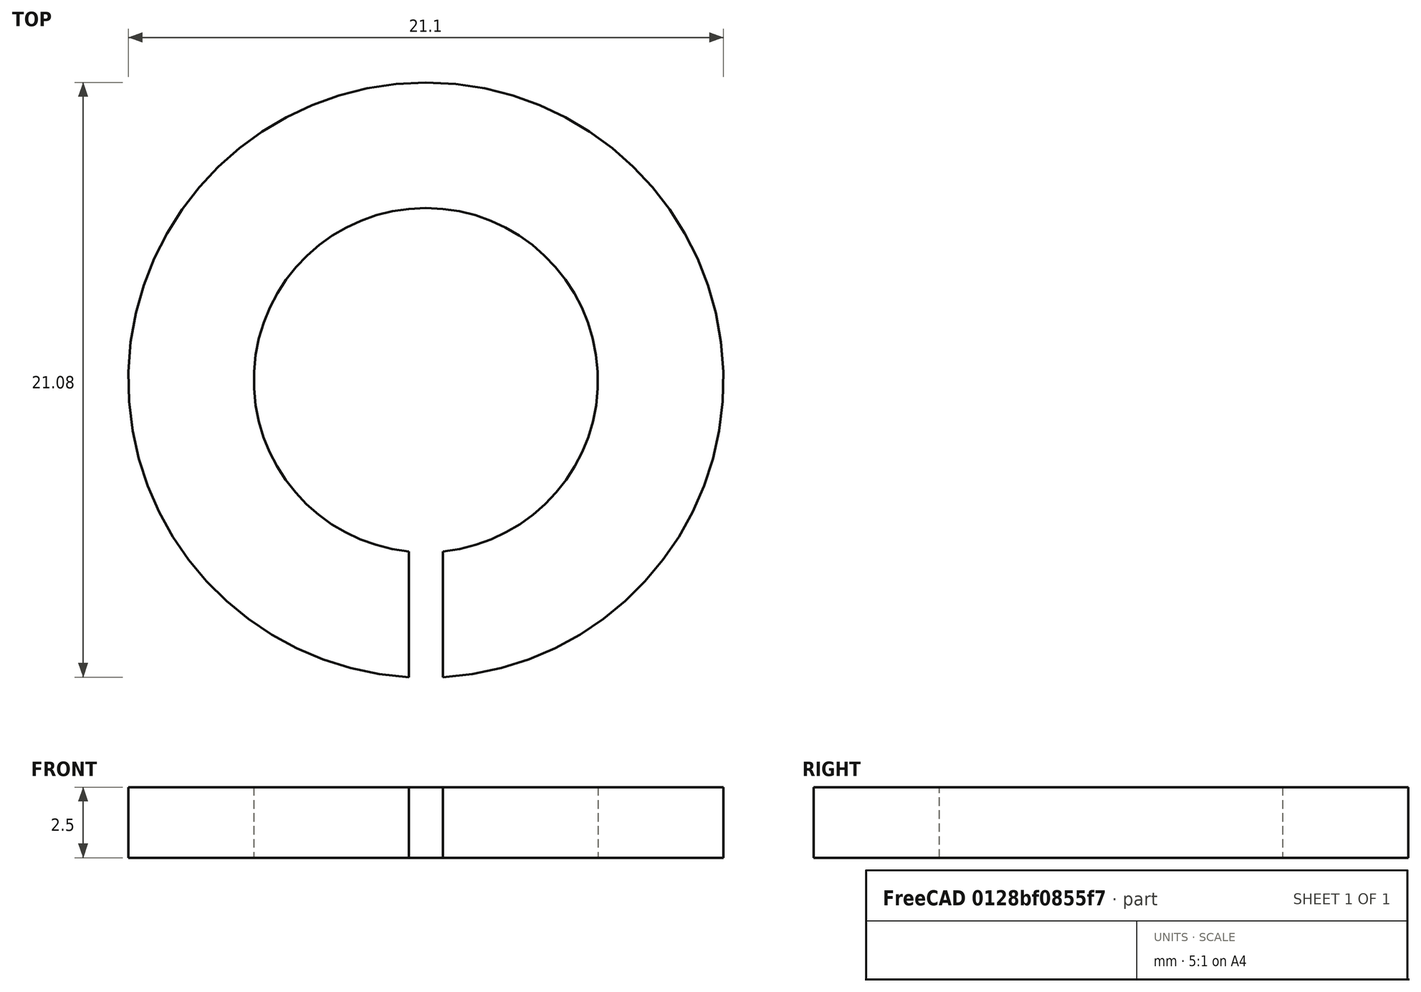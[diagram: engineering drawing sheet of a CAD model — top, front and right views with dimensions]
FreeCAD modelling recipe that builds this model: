
FCSTD DOCUMENT  (FreeCAD 0.15R4651 (Git))
Label: Federring_DIN127-A12
License: All rights reserved
LicenseURL: http://de.wikipedia.org/wiki/Alle_Rechte_vorbehalten
objects: Sketcher::SketchObject×1, PartDesign::Pad×1
note: 3 computed .brp shape members not serialized (recipe doc carries the construction recipe); baked Part::Feature solids carry a one-line shape summary decoded from their .brp

FEATURE [Sketcher::SketchObject] Sketch
  sketch-geometry (4):
    g0: ArcOfCircle CenterX=0 CenterY=0 CenterZ=0 NormalX=0 NormalY=0 NormalZ=1 Radius=6.1 StartAngle=4.81091 EndAngle=10.8971
    g1: ArcOfCircle CenterX=0 CenterY=0 CenterZ=0 NormalX=0 NormalY=0 NormalZ=1 Radius=10.55 StartAngle=4.76929 EndAngle=10.9387
    g2: LineSegment StartX=0.6 StartY=-6.07042 StartZ=0 EndX=0.6 EndY=-10.5329 EndZ=0
    g3: LineSegment StartX=-0.6 StartY=-10.5329 StartZ=0 EndX=-0.6 EndY=-6.07042 EndZ=0
  constraints (12):
    c: Coincident(g0,g-1)
    c: Coincident(g1,g-1)
    c: Vertical(g2)
    c: Vertical(g3)
    c: Coincident(g0,g2)
    c: Coincident(g0,g3)
    c: Coincident(g1,g2)
    c: Coincident(g1,g3)
    c: Symmetric(g1,g1,g-2)
    c: Radius(g0) = 6.1
    c: Radius(g1) = 10.55
    c: DistanceX(g1,g1) = -1.2
FEATURE [PartDesign::Pad] Pad  label="Federring DIN 127-A 12 #"
  Length = 2.5
  Length2 = 100
  Midplane = true
  Sketch = -> Sketch
  Type = 0
